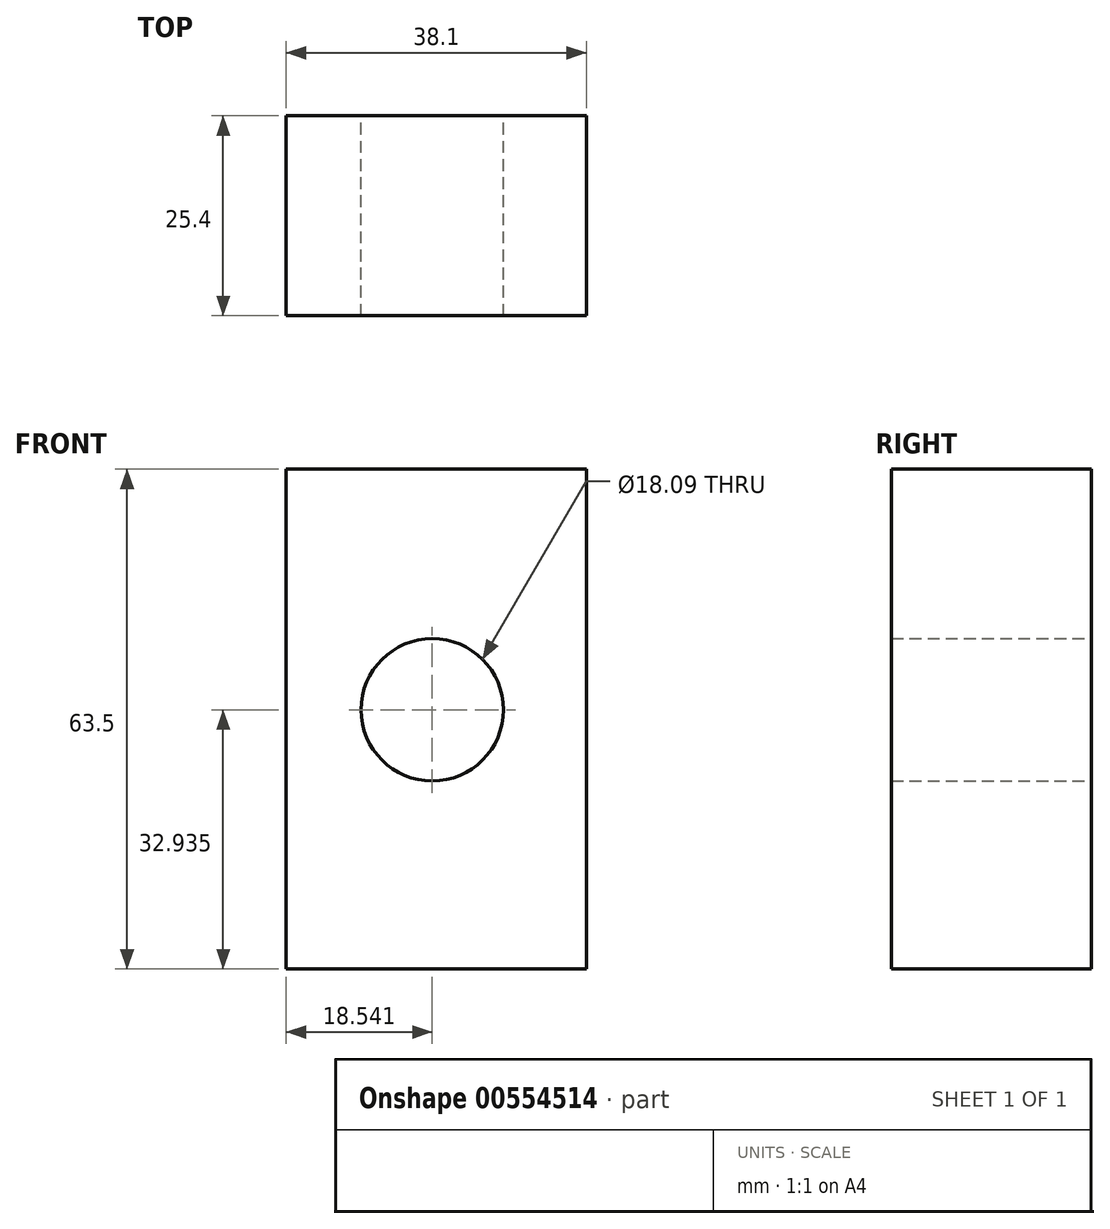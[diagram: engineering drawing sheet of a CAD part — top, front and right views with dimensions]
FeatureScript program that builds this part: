
annotation { "Feature Type Name" : "Feature", "Feature Type Description" : "" }
export const myFeature = defineFeature(function(context is Context, id is Id, definition is map)
    precondition{}
    {
        {
            var Q0;
            Q0=qCreatedBy(makeId("Front.planeOp"),FACE);
            var sketch = newSketch(context, id + "F0", { "sketchPlane" : qUnion([Q0])});
            skLineSegment(sketch, "E0.bottom", {"start": v(-47.75, 35.26) * mm, "end": v(-9.65, 35.26) * mm});
            skLineSegment(sketch, "E0.top", {"start": v(-47.75, -28.24) * mm, "end": v(-9.65, -28.24) * mm});
            skLineSegment(sketch, "E0.left", {"start": v(-47.75, 35.26) * mm, "end": v(-47.75, -28.24) * mm});
            skLineSegment(sketch, "E0.right", {"start": v(-9.65, 35.26) * mm, "end": v(-9.65, -28.24) * mm});
            skCircle(sketch, "E1", {"center": v(-29.2, 4.7) * mm, "radius": 9.04 * mm});
            skSolve(sketch);
        }
        {
            var Q0;
            Q0=makeQuery(id+"F0.imprint","IMPRINT",FACE,{"disambiguationData":[TD([[makeQuery(id+"F0.imprint","IMPRINT",EDGE,{"derivedFrom":sQuery(id+"F0.wireOp",EDGE,"E0.bottom")}),-1.0]])]});
            extrude(context, id + "F1", {"entities" : qUnion([Q0]), "depth" : 25.4 * mm, "offsetDistance" : 25.4 * mm});
        }
    });
